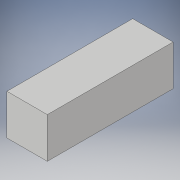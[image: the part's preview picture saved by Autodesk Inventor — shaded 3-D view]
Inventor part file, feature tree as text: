
AUTODESK INVENTOR PART (.ipt)
format: ipt  version: 2019 (Build 230136000, 136)  size: 129,536 bytes
history: native  units: mm
features: sketch x5, extrude x4
ambient origin geometry x8: Origin, YZ Plane, XZ Plane, XY Plane, X Axis, Y Axis, Z Axis, Center Point
bodies: Solid1 (feature_tree)
feature tree (9):
  extrude  "Extrusion1"  Depth=22.5mm
  extrude  "Extrusion2"  Depth=2.0mm
  extrude  "Extrusion3"  Depth=20.5mm
  sketch  "Sketch4"  dims[d6=20.5mm d7=2.0mm]
  extrude  "Extrusion4"  Depth=2.0mm
  sketch  "Sketch1"  dims[d0=22.5mm d1=22.5mm]
  sketch  "Sketch2"  dims[d2=20.5mm d3=2.0mm]
  sketch  "Sketch3"  dims[d4=2.0mm d5=20.5mm]
  sketch  "Sketch5"  dims[d8=2.0mm d9=20.5mm d10=18.5mm d11=18.5mm d12=69.0mm d13=0.0mm d14=2.0mm d15=67.0mm d16=18.5mm d17=66.0mm d18=18.5mm d19=0.0mm d20=22.5mm d21=22.5mm d22=1.0mm d23=0.0mm d24=18.5mm d25=66.0mm d26=2.0mm d27=0.0mm]
